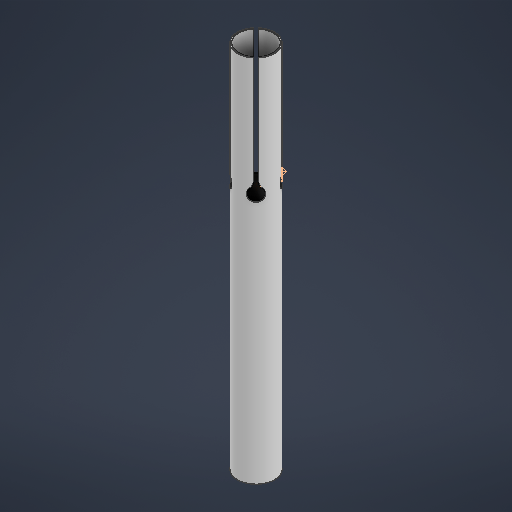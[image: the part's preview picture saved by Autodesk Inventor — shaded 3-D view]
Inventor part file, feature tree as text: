
AUTODESK INVENTOR PART (.ipt)
format: ipt  version: 2025 (Build 290162010, 162A)  size: 293,376 bytes
history: native  units: mm
features: extrude x3, sketch x3, other x2, plane x1, fillet x1, mirror x1
ambient origin geometry x8: Origin, YZ Plane, XZ Plane, XY Plane, X Axis, Y Axis, Z Axis, Center Point
bodies: Solid1 (feature_tree)
feature tree (11):
  extrude  "Extrusion1"  Depth=2.54mm
  extrude  "Extrusion2"  TaperAngle=45.0deg  [1 undecoded]
  other  "Work Point1"
  other  "Work Point2"
  plane  "Work Plane1"
  extrude  "Extrusion3"  Depth=19.5mm
  fillet  "Fillet1"  Radius=3.5mm
  mirror  "Mirror1"
  sketch  "Sketch1"  dims[d0=76.2mm d1=2.54mm]
  sketch  "Sketch2"  dims[d2=762.0mm d3=0.0mm d4=45.0deg]
  sketch  "Sketch3"  dims[d5=3.5mm d6=3.5mm d7=3.5mm d8=3.5mm d9=3.5mm d10=3.5mm d11=230.2mm d12=0.0mm d13=14.0mm d14=28.0mm d15=230.2mm d16=0.0mm d17=19.5mm]
note: 1 required parameter value undecoded (feature->parameter linkage not recoverable at this tier; creation-order binding heuristic only, values carry confidence <= 0.55)
